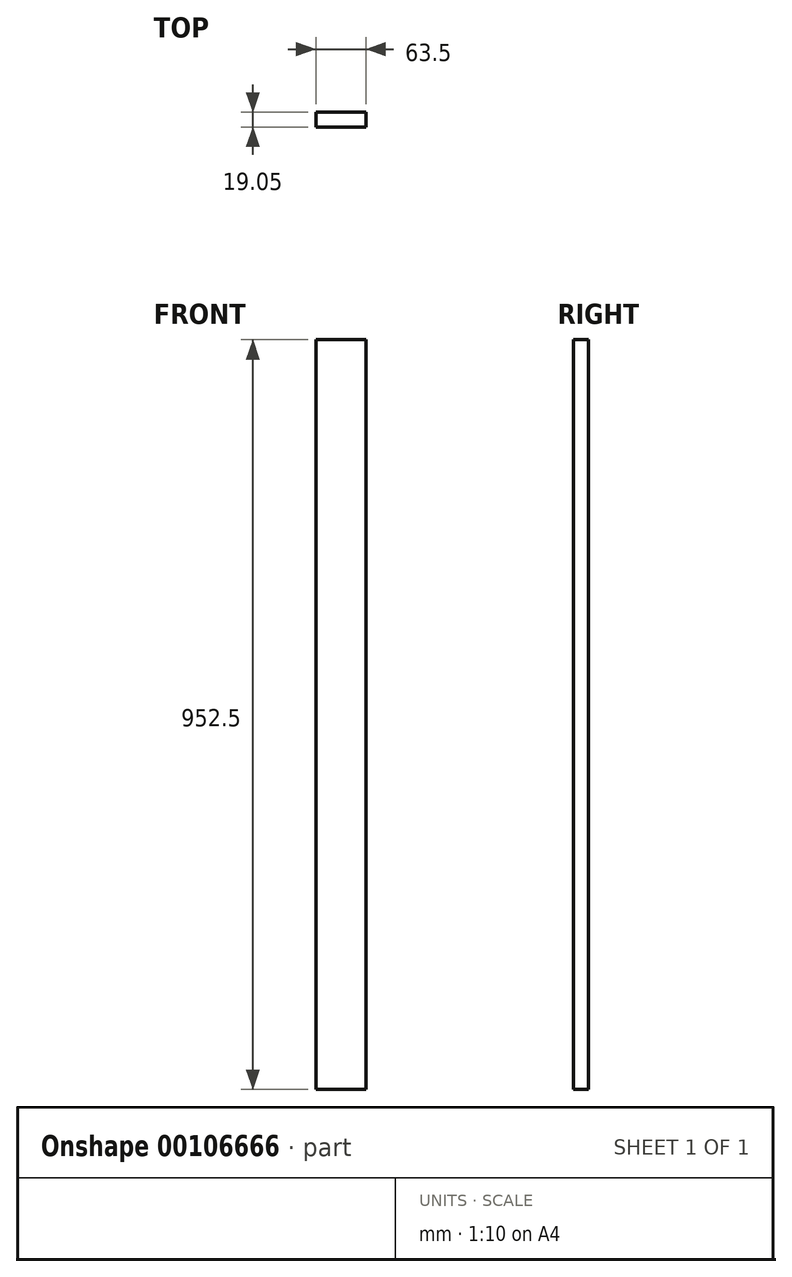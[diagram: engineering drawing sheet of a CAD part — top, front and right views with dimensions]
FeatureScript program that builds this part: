
annotation { "Feature Type Name" : "Feature", "Feature Type Description" : "" }
export const myFeature = defineFeature(function(context is Context, id is Id, definition is map)
    precondition{}
    {
        {
            var Q0;
            Q0=qCreatedBy(makeId("Front.planeOp"),FACE);
            var sketch = newSketch(context, id + "F0", { "sketchPlane" : qUnion([Q0])});
            skLineSegment(sketch, "E0.bottom", {"start": v(0, 0) * mm, "end": v(63.5, 0) * mm});
            skLineSegment(sketch, "E0.top", {"start": v(0, 952.5) * mm, "end": v(63.5, 952.5) * mm});
            skLineSegment(sketch, "E0.left", {"start": v(0, 0) * mm, "end": v(0, 952.5) * mm});
            skLineSegment(sketch, "E0.right", {"start": v(63.5, 0) * mm, "end": v(63.5, 952.5) * mm});
            skSolve(sketch);
        }
        {
            var Q0;
            Q0=makeQuery(id+"F0.imprint","IMPRINT",FACE,{"disambiguationData":[TD([[makeQuery(id+"F0.imprint","IMPRINT",EDGE,{"derivedFrom":sQuery(id+"F0.wireOp",EDGE,"E0.bottom")}),1.0]])]});
            extrude(context, id + "F1", {"entities" : qUnion([Q0]), "depth" : 19.05 * mm});
        }
    });
